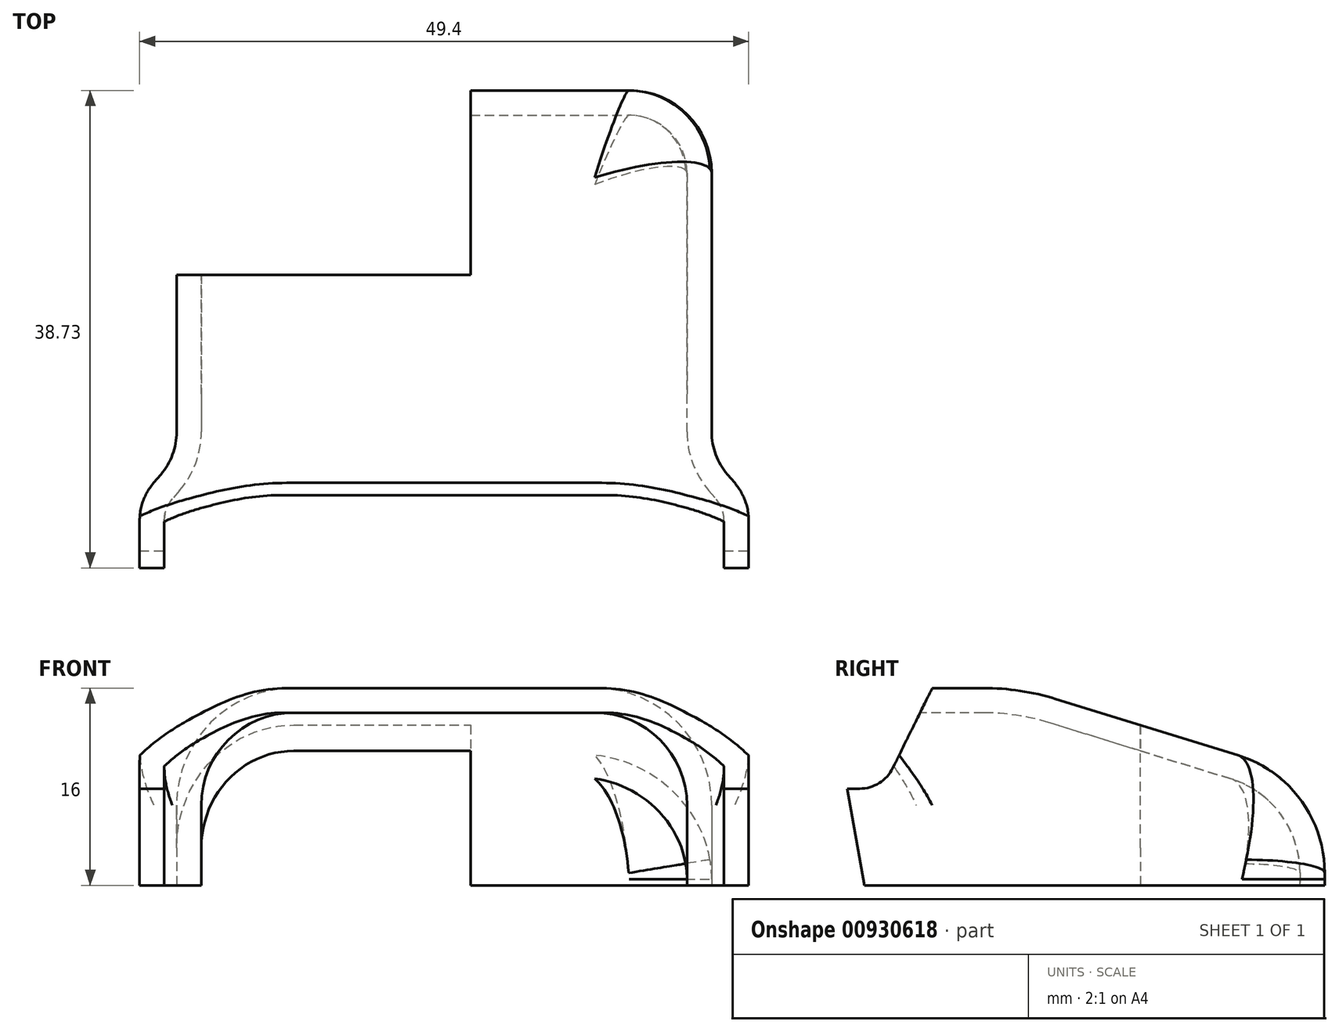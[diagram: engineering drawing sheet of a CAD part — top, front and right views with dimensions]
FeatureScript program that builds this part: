
annotation { "Feature Type Name" : "Feature", "Feature Type Description" : "" }
export const myFeature = defineFeature(function(context is Context, id is Id, definition is map)
    precondition{}
    {
        {
            var Q0;
            Q0=qCreatedBy(makeId("Top.planeOp"),FACE);
            var sketch = newSketch(context, id + "F0", { "sketchPlane" : qUnion([Q0])});
            skLineSegment(sketch, "E0", {"start": v(-22, 0.3) * mm, "end": v(-22, 10) * mm, "construction": true});
            skLineSegment(sketch, "E1", {"start": v(-22, 10) * mm, "end": v(-32, 10) * mm, "construction": true});
            skLineSegment(sketch, "E2", {"start": v(22, 0.3) * mm, "end": v(22, 17.95) * mm, "construction": true});
            skLineSegment(sketch, "E3", {"start": v(20, 0.3) * mm, "end": v(20, 17.95) * mm, "construction": true});
            skLineSegment(sketch, "E4", {"start": v(-20, 0.3) * mm, "end": v(-20, 10) * mm, "construction": true});
            skLineSegment(sketch, "E5", {"start": v(-22, 12) * mm, "end": v(-32, 12) * mm, "construction": true});
            skPoint(sketch, "E6.visualSharp", {"position": v(-20, 12) * mm});
            skArc(sketch, "E6.filletArc", {"start": v(-20, 10) * mm, "mid": v(-20.59, 11.41) * mm, "end": v(-22, 12) * mm, "construction": true});
            skLineSegment(sketch, "E7", {"start": v(-22, 0.3) * mm, "end": v(-20, 0.3) * mm, "construction": true});
            skLineSegment(sketch, "E8", {"start": v(20, 0.3) * mm, "end": v(22, 0.3) * mm, "construction": true});
            skPoint(sketch, "E9.start.orphan", {"position": v(-22, 0) * mm});
            skPoint(sketch, "E10.orphan", {"position": v(22, 0) * mm});
            skArc(sketch, "E11", {"start": v(22, 17.95) * mm, "mid": v(19.95, 22.9) * mm, "end": v(15, 24.94) * mm, "construction": true});
            skArc(sketch, "E12", {"start": v(20, 17.95) * mm, "mid": v(18.54, 21.48) * mm, "end": v(15, 22.94) * mm, "construction": true});
            skLineSegment(sketch, "E13", {"start": v(15, 24.94) * mm, "end": v(1.85, 24.94) * mm, "construction": true});
            skLineSegment(sketch, "E14", {"start": v(1.85, 24.94) * mm, "end": v(1.85, 34.95) * mm, "construction": true});
            skLineSegment(sketch, "E15", {"start": v(-0.15, 34.95) * mm, "end": v(-0.15, 24.94) * mm, "construction": true});
            skLineSegment(sketch, "E16", {"start": v(15, 22.94) * mm, "end": v(1.86, 22.94) * mm, "construction": true});
            skArc(sketch, "E17", {"start": v(-0.15, 24.94) * mm, "mid": v(0.44, 23.53) * mm, "end": v(1.86, 22.94) * mm, "construction": true});
            skLineSegment(sketch, "E18", {"start": v(-22, -0.3) * mm, "end": v(-20, -0.3) * mm, "construction": true});
            skLineSegment(sketch, "E19", {"start": v(-20, -0.3) * mm, "end": v(-20, -13) * mm, "construction": true});
            skLineSegment(sketch, "E20", {"start": v(20, -0.3) * mm, "end": v(22, -0.3) * mm, "construction": true});
            skLineSegment(sketch, "E21", {"start": v(20, -0.3) * mm, "end": v(20, -13) * mm, "construction": true});
            skLineSegment(sketch, "E22", {"start": v(20, -13) * mm, "end": v(25, -13) * mm, "construction": true});
            skLineSegment(sketch, "E23", {"start": v(-25, -13) * mm, "end": v(-20, -13) * mm, "construction": true});
            skLineSegment(sketch, "E24", {"start": v(-32, 10) * mm, "end": v(-32, 12) * mm, "construction": true});
            skLineSegment(sketch, "E25", {"start": v(1.85, 34.95) * mm, "end": v(-0.15, 34.95) * mm, "construction": true});
            skLineSegment(sketch, "E26", {"start": v(-25, -13) * mm, "end": v(-25, -10.25) * mm, "construction": true});
            skLineSegment(sketch, "E27", {"start": v(-22, -0.3) * mm, "end": v(-22, -3.05) * mm, "construction": true});
            skLineSegment(sketch, "E28", {"start": v(-23.2, -6.3) * mm, "end": v(-23.8, -7) * mm, "construction": true});
            skLineSegment(sketch, "E29", {"start": v(22, -0.3) * mm, "end": v(22, -3.05) * mm, "construction": true});
            skLineSegment(sketch, "E30", {"start": v(25, -13) * mm, "end": v(25, -10.25) * mm, "construction": true});
            skLineSegment(sketch, "E31", {"start": v(23.8, -7) * mm, "end": v(23.2, -6.3) * mm, "construction": true});
            skArc(sketch, "E32", {"start": v(-23.2, -6.3) * mm, "mid": v(-22.31, -4.79) * mm, "end": v(-22, -3.05) * mm, "construction": true});
            skArc(sketch, "E33", {"start": v(-23.8, -7) * mm, "mid": v(-24.69, -8.51) * mm, "end": v(-25, -10.25) * mm, "construction": true});
            skArc(sketch, "E34", {"start": v(22, -3.05) * mm, "mid": v(22.31, -4.79) * mm, "end": v(23.2, -6.3) * mm, "construction": true});
            skArc(sketch, "E35", {"start": v(25, -10.25) * mm, "mid": v(24.69, -8.51) * mm, "end": v(23.8, -7) * mm, "construction": true});
            skSolve(sketch);
        }
        {
            var Q0;
            Q0=qCreatedBy(makeId("Top.planeOp"),FACE);
            var sketch = newSketch(context, id + "F1", { "sketchPlane" : qUnion([Q0])});
            skLineSegment(sketch, "E36", {"start": v(-21.7, 9.7) * mm, "end": v(-21.7, -3.05) * mm});
            skLineSegment(sketch, "E37", {"start": v(21.7, -3.05) * mm, "end": v(21.7, 17.95) * mm});
            skLineSegment(sketch, "E38", {"start": v(-21.7, 9.7) * mm, "end": v(2.15, 9.7) * mm});
            skLineSegment(sketch, "E39", {"start": v(2.15, 9.7) * mm, "end": v(2.15, 24.64) * mm});
            skLineSegment(sketch, "E40", {"start": v(2.15, 24.64) * mm, "end": v(15, 24.64) * mm});
            skArc(sketch, "E41", {"start": v(21.7, 17.95) * mm, "mid": v(19.74, 22.68) * mm, "end": v(15, 24.64) * mm});
            skArc(sketch, "E42", {"start": v(-22.98, -6.5) * mm, "mid": v(-22.03, -4.9) * mm, "end": v(-21.7, -3.05) * mm});
            skLineSegment(sketch, "E43", {"start": v(-22.98, -6.5) * mm, "end": v(-23.57, -7.19) * mm});
            skArc(sketch, "E44", {"start": v(-23.57, -7.19) * mm, "mid": v(-24.4, -8.62) * mm, "end": v(-24.7, -10.25) * mm});
            skLineSegment(sketch, "E45", {"start": v(-24.7, -10.25) * mm, "end": v(-24.7, -18) * mm});
            skArc(sketch, "E46", {"start": v(21.7, -3.05) * mm, "mid": v(22.03, -4.9) * mm, "end": v(22.98, -6.5) * mm});
            skLineSegment(sketch, "E47", {"start": v(22.98, -6.5) * mm, "end": v(23.57, -7.19) * mm});
            skArc(sketch, "E48", {"start": v(24.7, -10.25) * mm, "mid": v(24.4, -8.62) * mm, "end": v(23.57, -7.19) * mm});
            skLineSegment(sketch, "E49", {"start": v(24.7, -10.25) * mm, "end": v(24.7, -18) * mm});
            skLineSegment(sketch, "E50", {"start": v(24.7, -18) * mm, "end": v(-24.7, -18) * mm});
            skSolve(sketch);
        }
        {
            var Q0;
            Q0=qSketchRegion(id+"F1",true);
            extrude(context, id + "F2", {"entities" : qUnion([Q0]), "depth" : 16 * mm, "offsetDistance" : 25 * mm});
        }
        {
            var Q0;
            Q0=makeQuery(id+"F2.opExtrude","SWEPT_FACE",FACE,{"disambiguationData":[OSD([sQuery(id+"F1.wireOp",EDGE,"E49")])]});
            var sketch = newSketch(context, id + "F3", { "sketchPlane" : qUnion([Q0])});
            skLineSegment(sketch, "E51", {"start": v(24.64, 16) * mm, "end": v(24.64, 1) * mm});
            skArc(sketch, "E52", {"start": v(24.64, 1) * mm, "mid": v(22.7, 6.94) * mm, "end": v(17.6, 10.55) * mm});
            skLineSegment(sketch, "E53", {"start": v(17.6, 10.55) * mm, "end": v(2.85, 15.1) * mm});
            skArc(sketch, "E54", {"start": v(2.85, 15.1) * mm, "mid": v(-0.07, 15.78) * mm, "end": v(-3.05, 16) * mm});
            skPoint(sketch, "E55.orphan", {"position": v(24.64, 0) * mm});
            skLineSegment(sketch, "E56", {"start": v(-3.05, 16) * mm, "end": v(24.64, 16) * mm});
            skLineSegment(sketch, "E57", {"start": v(-12.7, 0) * mm, "end": v(-14.08, 7.84) * mm});
            skLineSegment(sketch, "E58", {"start": v(-14.08, 7.84) * mm, "end": v(-13.08, 7.84) * mm});
            skLineSegment(sketch, "E59", {"start": v(-7.19, 16) * mm, "end": v(-10.4, 9.51) * mm});
            skArc(sketch, "E60", {"start": v(-13.08, 7.84) * mm, "mid": v(-11.5, 8.3) * mm, "end": v(-10.4, 9.51) * mm});
            skLineSegment(sketch, "E61", {"start": v(-7.19, 16) * mm, "end": v(-18, 16) * mm});
            skLineSegment(sketch, "E62", {"start": v(-18, 16) * mm, "end": v(-18, 0) * mm});
            skLineSegment(sketch, "E63", {"start": v(-18, 0) * mm, "end": v(-12.7, 0) * mm});
            skSolve(sketch);
        }
        {
            var Q0;
            Q0=qSketchRegion(id+"F3",true);
            var Q1;
            Q1=makeQuery(id+"F2.opExtrude","SWEPT_FACE",FACE,{"disambiguationData":[OSD([sQuery(id+"F1.wireOp",EDGE,"E45")])]});
            extrude(context, id + "F4", {"entities" : qUnion([Q0]), "operationType" : NewBodyOperationType.REMOVE, "endBound" : BoundingType.UP_TO_SURFACE, "oppositeDirection" : true, "depth" : 25 * mm, "endBoundEntityFace" : qUnion([Q1]), "offsetDistance" : 25 * mm});
        }
        {
            var Q0;
            Q0=makeQuery(id+"F4.boolean.opBoolean","INTERSECT",EDGE,{"derivedFrom":[makeQuery(id+"F2.opExtrude","SWEPT_FACE",FACE,{"disambiguationData":[OSD([sQuery(id+"F1.wireOp",EDGE,"E37")])]}),makeQuery(id+"F4.opExtrude","SWEPT_FACE",FACE,{"disambiguationData":[OSD([sQuery(id+"F3.wireOp",EDGE,"E53")])]})]});
            var Q1;
            Q1=makeQuery(id+"F4.boolean.opBoolean","INTERSECT",EDGE,{"derivedFrom":[makeQuery(id+"F2.opExtrude","SWEPT_FACE",FACE,{"disambiguationData":[OSD([sQuery(id+"F1.wireOp",EDGE,"E36")])]}),makeQuery(id+"F4.opExtrude","SWEPT_FACE",FACE,{"disambiguationData":[OSD([sQuery(id+"F3.wireOp",EDGE,"E53")])]})]});
            fillet(context, id + "F5", {"entities" : qUnion([Q0, Q1]), "radius" : 9.5 * mm, "tangentPropagation" : true, "allowEdgeOverflow" : false});
        }
        {
            var Q0;
            Q0=makeQuery(id+"F2.opExtrude","CAP_FACE",FACE,{"disambiguationData":[OSD([sQuery(id+"F1.wireOp",EDGE,"E36"),sQuery(id+"F1.wireOp",EDGE,"E37"),sQuery(id+"F1.wireOp",EDGE,"E38"),sQuery(id+"F1.wireOp",EDGE,"E39"),sQuery(id+"F1.wireOp",EDGE,"E40"),sQuery(id+"F1.wireOp",EDGE,"E41"),sQuery(id+"F1.wireOp",EDGE,"E42"),sQuery(id+"F1.wireOp",EDGE,"E43"),sQuery(id+"F1.wireOp",EDGE,"E44"),sQuery(id+"F1.wireOp",EDGE,"E45"),sQuery(id+"F1.wireOp",EDGE,"E46"),sQuery(id+"F1.wireOp",EDGE,"E47"),sQuery(id+"F1.wireOp",EDGE,"E48"),sQuery(id+"F1.wireOp",EDGE,"E49"),sQuery(id+"F1.wireOp",EDGE,"E50")])],"isStart":true});
            var Q1;
            Q1=makeQuery(id+"F4.boolean.opBoolean","COPY",FACE,{"derivedFrom":makeQuery(id+"F4.opExtrude","SWEPT_FACE",FACE,{"disambiguationData":[OSD([sQuery(id+"F3.wireOp",EDGE,"E57")])]})});
            var Q2;
            Q2=makeQuery(id+"F4.boolean.opBoolean","COPY",FACE,{"derivedFrom":makeQuery(id+"F4.opExtrude","SWEPT_FACE",FACE,{"disambiguationData":[OSD([sQuery(id+"F3.wireOp",EDGE,"E60")])]})});
            var Q3;
            Q3=makeQuery(id+"F4.boolean.opBoolean","COPY",FACE,{"derivedFrom":makeQuery(id+"F4.opExtrude","SWEPT_FACE",FACE,{"disambiguationData":[OSD([sQuery(id+"F3.wireOp",EDGE,"E59")])]})});
            var Q4;
            Q4=makeQuery(id+"F4.boolean.opBoolean","COPY",FACE,{"derivedFrom":makeQuery(id+"F4.opExtrude","SWEPT_FACE",FACE,{"disambiguationData":[OSD([sQuery(id+"F3.wireOp",EDGE,"E58")])]})});
            var Q5;
            Q5=makeQuery(id+"F2.opExtrude","SWEPT_FACE",FACE,{"disambiguationData":[OSD([sQuery(id+"F1.wireOp",EDGE,"E38")])]});
            var Q6;
            Q6=makeQuery(id+"F2.opExtrude","SWEPT_FACE",FACE,{"disambiguationData":[OSD([sQuery(id+"F1.wireOp",EDGE,"E39")])]});
            shell(context, id + "F6", {"entities" : qUnion([Q0, Q1, Q2, Q3, Q4, Q5, Q6]), "thickness" : 2 * mm});
        }
    });
